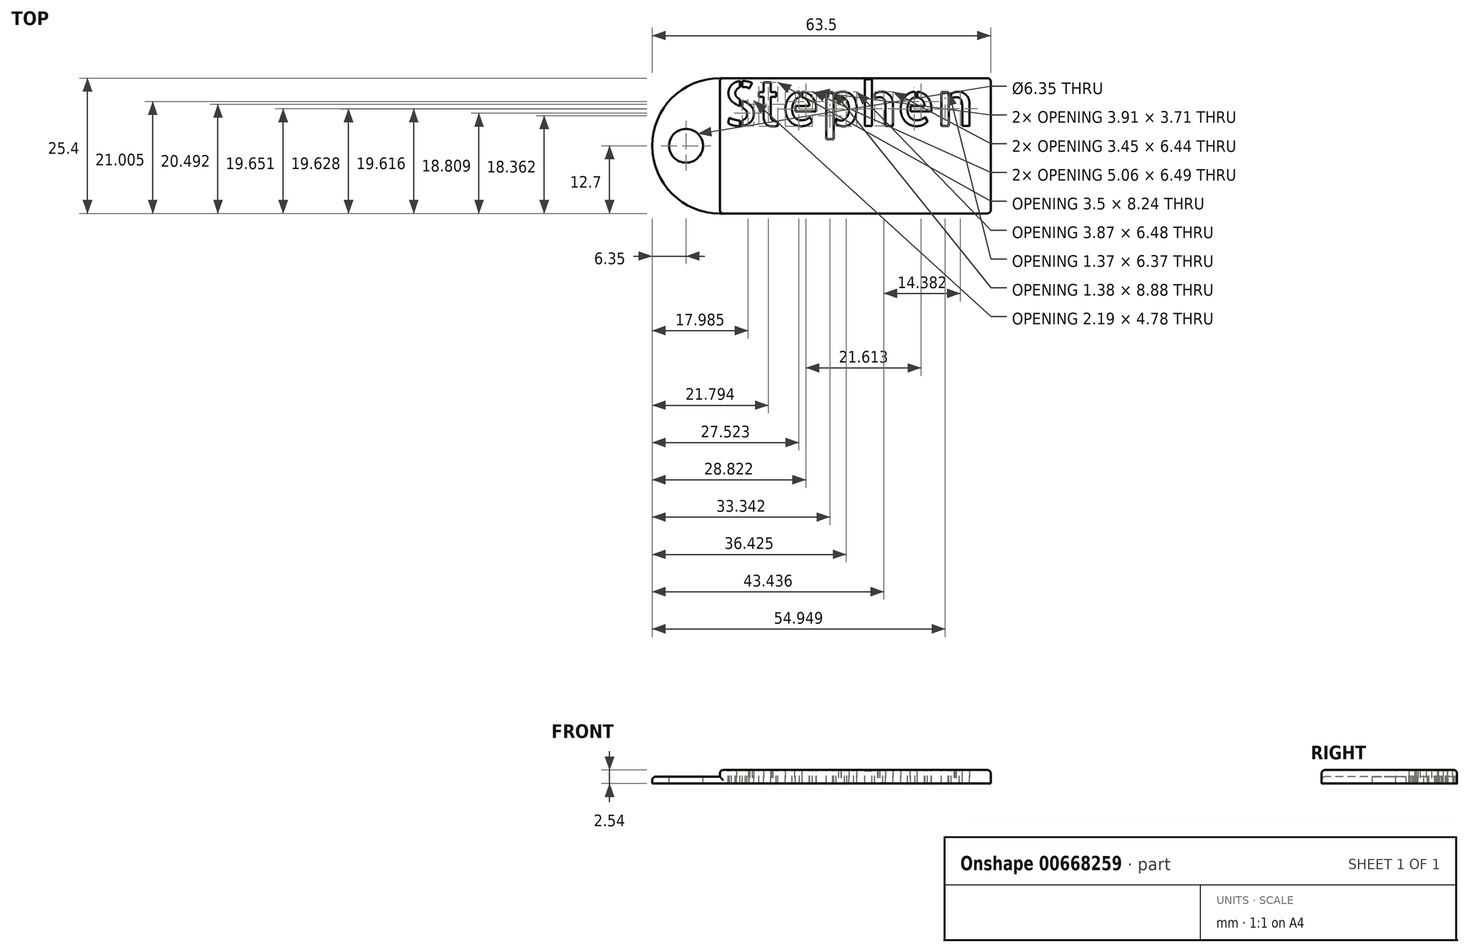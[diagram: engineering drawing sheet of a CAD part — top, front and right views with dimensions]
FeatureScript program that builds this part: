
annotation { "Feature Type Name" : "Feature", "Feature Type Description" : "" }
export const myFeature = defineFeature(function(context is Context, id is Id, definition is map)
    precondition{}
    {
        {
            var Q0;
            Q0=qCreatedBy(makeId("Top.planeOp"),FACE);
            var sketch = newSketch(context, id + "F0", { "sketchPlane" : qUnion([Q0])});
            skLineSegment(sketch, "E0.bottom", {"start": v(25.4, 12.7) * mm, "end": v(-25.4, 12.7) * mm});
            skLineSegment(sketch, "E0.top", {"start": v(25.4, -12.7) * mm, "end": v(-25.4, -12.7) * mm});
            skLineSegment(sketch, "E0.left", {"start": v(25.4, 12.7) * mm, "end": v(25.4, -12.7) * mm});
            skPoint(sketch, "E0.middle", {"position": v(0, 0) * mm});
            skArc(sketch, "E1", {"start": v(-25.4, 12.7) * mm, "mid": v(-38.1, 0) * mm, "end": v(-25.4, -12.7) * mm});
            skSolve(sketch);
        }
        {
            var Q0;
            Q0 = qSketchRegion(id + "F0", true);
            extrude(context, id + "F1", {"entities" : qUnion([Q0]), "depth" : 1.27 * mm, "offsetDistance" : 25.4 * mm});
        }
        {
            var Q0;
            Q0=makeQuery(id+"F1.opExtrude","CAP_FACE",FACE,{"disambiguationData":[OSD([sQuery(id+"F0.wireOp",EDGE,"E0.bottom"),sQuery(id+"F0.wireOp",EDGE,"E0.top"),sQuery(id+"F0.wireOp",EDGE,"E0.left"),sQuery(id+"F0.wireOp",EDGE,"E1")])],"isStart":false});
            var sketch = newSketch(context, id + "F2", { "sketchPlane" : qUnion([Q0])});
            skLineSegment(sketch, "E2.bottom", {"start": v(25.4, 12.7) * mm, "end": v(-25.4, 12.7) * mm});
            skLineSegment(sketch, "E2.top", {"start": v(25.4, -12.7) * mm, "end": v(-25.4, -12.7) * mm});
            skLineSegment(sketch, "E2.left", {"start": v(25.4, 12.7) * mm, "end": v(25.4, -12.7) * mm});
            skLineSegment(sketch, "E2.right", {"start": v(-25.4, 12.7) * mm, "end": v(-25.4, -12.7) * mm});
            skPoint(sketch, "E2.middle", {"position": v(0, 0) * mm});
            skSolve(sketch);
        }
        {
            var Q0;
            Q0 = qSketchRegion(id + "F2", true);
            extrude(context, id + "F3", {"entities" : qUnion([Q0]), "operationType" : NewBodyOperationType.ADD, "depth" : 1.27 * mm, "offsetDistance" : 25.4 * mm});
        }
        {
            var Q0;
            Q0=makeQuery(id+"F1.opExtrude","CAP_FACE",FACE,{"disambiguationData":[OSD([sQuery(id+"F0.wireOp",EDGE,"E0.bottom"),sQuery(id+"F0.wireOp",EDGE,"E0.top"),sQuery(id+"F0.wireOp",EDGE,"E0.left"),sQuery(id+"F0.wireOp",EDGE,"E1")])],"isStart":false});
            var sketch = newSketch(context, id + "F4", { "sketchPlane" : qUnion([Q0])});
            skCircle(sketch, "E3", {"center": v(-31.75, 0) * mm, "radius": 3.18 * mm});
            skSolve(sketch);
        }
        {
            var Q0;
            Q0 = qSketchRegion(id + "F4", true);
            extrude(context, id + "F5", {"entities" : qUnion([Q0]), "operationType" : NewBodyOperationType.REMOVE, "oppositeDirection" : true, "depth" : 25.4 * mm, "offsetDistance" : 25.4 * mm});
        }
        {
            var Q0;
            Q0=makeQuery(id+"F3.opExtrude","CAP_EDGE",EDGE,{"disambiguationData":[OSD([sQuery(id+"F2.wireOp",EDGE,"E2.right")])],"isStart":false});
            var Q1;
            Q1=makeQuery(id+"F3.opExtrude","CAP_EDGE",EDGE,{"disambiguationData":[OSD([sQuery(id+"F2.wireOp",EDGE,"E2.bottom")])],"isStart":false});
            var Q2;
            Q2=makeQuery(id+"F3.opExtrude","CAP_EDGE",EDGE,{"disambiguationData":[OSD([sQuery(id+"F2.wireOp",EDGE,"E2.left")])],"isStart":false});
            var Q3;
            Q3=makeQuery(id+"F3.opExtrude","CAP_EDGE",EDGE,{"disambiguationData":[OSD([sQuery(id+"F2.wireOp",EDGE,"E2.top")])],"isStart":false});
            var Q4;
            Q4=makeQuery(id+"F1.opExtrude","CAP_EDGE",EDGE,{"disambiguationData":[OSD([sQuery(id+"F0.wireOp",EDGE,"E1")])],"isStart":false});
            var Q5;
            Q5=makeQuery(id+"F3.boolean.opBoolean","MERGE",EDGE,{"derivedFrom":[makeQuery(id+"F1.opExtrude","SWEPT_EDGE",EDGE,{"disambiguationData":[OSD([sQuery(id+"F0.wireOp",EDGE,"E0.top"),sQuery(id+"F0.wireOp",EDGE,"E0.left")])]}),makeQuery(id+"F3.opExtrude","SWEPT_EDGE",EDGE,{"disambiguationData":[OSD([sQuery(id+"F2.wireOp",EDGE,"E2.top"),sQuery(id+"F2.wireOp",EDGE,"E2.left")])]})]});
            var Q6;
            Q6=makeQuery(id+"F3.opExtrude","SWEPT_EDGE",EDGE,{"disambiguationData":[OSD([sQuery(id+"F0.wireOp",EDGE,"E1"),sQuery(id+"F2.wireOp",EDGE,"E2.top"),sQuery(id+"F2.wireOp",EDGE,"E2.right")])]});
            var Q7;
            Q7=makeQuery(id+"F3.opExtrude","CAP_EDGE",EDGE,{"disambiguationData":[OSD([sQuery(id+"F2.wireOp",EDGE,"E2.right")])],"isStart":true});
            var Q8;
            Q8=makeQuery(id+"F3.opExtrude","SWEPT_EDGE",EDGE,{"disambiguationData":[OSD([sQuery(id+"F0.wireOp",EDGE,"E1"),sQuery(id+"F2.wireOp",EDGE,"E2.bottom"),sQuery(id+"F2.wireOp",EDGE,"E2.right")])]});
            var Q9;
            Q9=makeQuery(id+"F3.boolean.opBoolean","MERGE",EDGE,{"derivedFrom":[makeQuery(id+"F1.opExtrude","SWEPT_EDGE",EDGE,{"disambiguationData":[OSD([sQuery(id+"F0.wireOp",EDGE,"E0.bottom"),sQuery(id+"F0.wireOp",EDGE,"E0.left")])]}),makeQuery(id+"F3.opExtrude","SWEPT_EDGE",EDGE,{"disambiguationData":[OSD([sQuery(id+"F2.wireOp",EDGE,"E2.bottom"),sQuery(id+"F2.wireOp",EDGE,"E2.left")])]})]});
            fillet(context, id + "F6", {"entities" : qUnion([Q0, Q1, Q2, Q3, Q4, Q5, Q6, Q7, Q8, Q9]), "radius" : 0.64 * mm, "tangentPropagation" : true, "allowEdgeOverflow" : false});
        }
        {
            var Q0;
            Q0=makeQuery(id+"F3.opExtrude","CAP_FACE",FACE,{"disambiguationData":[OSD([sQuery(id+"F2.wireOp",EDGE,"E2.bottom"),sQuery(id+"F2.wireOp",EDGE,"E2.top"),sQuery(id+"F2.wireOp",EDGE,"E2.left"),sQuery(id+"F2.wireOp",EDGE,"E2.right")])],"isStart":false});
            var sketch = newSketch(context, id + "F7", { "sketchPlane" : qUnion([Q0])});
            skText(sketch, "E4", { "text": "Stephen", "fontName": "AllertaStencil-Regular.ttf"});
            const initialGuessF7  = {"E4": [-0.02477, 0.00373, 1, 0, 0.00833]};
            skSetInitialGuess(sketch, initialGuessF7);
            skSolve(sketch);
        }
        {
            var Q0;
            Q0 = qSketchRegion(id + "F7", true);
            extrude(context, id + "F8", {"entities" : qUnion([Q0]), "operationType" : NewBodyOperationType.REMOVE, "oppositeDirection" : true, "depth" : 25.4 * mm, "offsetDistance" : 25.4 * mm});
        }
    });
